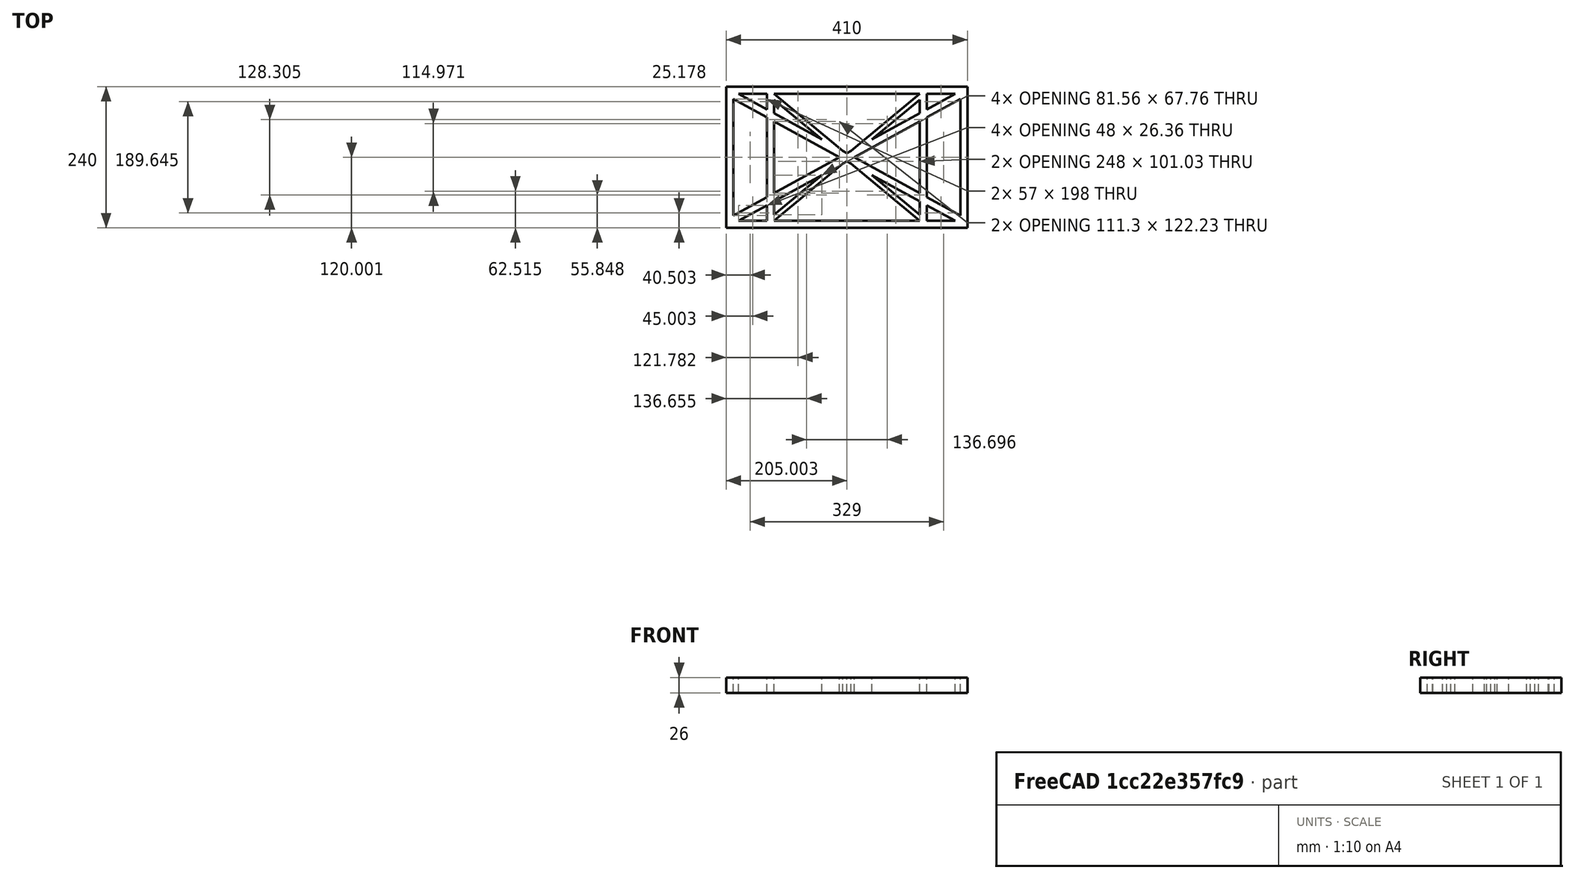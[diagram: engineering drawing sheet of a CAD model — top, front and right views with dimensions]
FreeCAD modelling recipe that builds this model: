
FCSTD DOCUMENT  (FreeCAD 0.19R0.19.2)
Label: laptopStand030
License: All rights reserved
LicenseURL: http://en.wikipedia.org/wiki/All_rights_reserved
objects: Sketcher::SketchObject×3, Part::Extrusion×1
note: 4 computed .brp shape members not serialized (recipe doc carries the construction recipe); baked Part::Feature solids carry a one-line shape summary decoded from their .brp

FEATURE [Sketcher::SketchObject] Sketch
  FullyConstrained = true
  sketch-geometry (52):
    g0: LineSegment StartX=-22.9272 StartY=136.221 StartZ=0 EndX=-22.9272 EndY=-103.779 EndZ=0
    g1: LineSegment StartX=-22.9272 StartY=136.221 StartZ=0 EndX=387.073 EndY=136.221 EndZ=0
    g2: LineSegment StartX=-22.9272 StartY=-103.779 StartZ=0 EndX=387.073 EndY=-103.779 EndZ=0
    g3: LineSegment StartX=387.073 StartY=136.221 StartZ=0 EndX=387.073 EndY=-103.779 EndZ=0
    g4: LineSegment StartX=375.073 StartY=115.221 StartZ=0 EndX=318.073 EndY=83.9235 EndZ=0
    g5: LineSegment StartX=-10.9272 StartY=-82.7794 StartZ=0 EndX=46.0728 EndY=-51.4823 EndZ=0
    g6: LineSegment StartX=-1.92719 StartY=124.221 StartZ=0 EndX=46.0728 EndY=97.8651 EndZ=0
    g7: LineSegment StartX=366.073 StartY=-91.7794 StartZ=0 EndX=318.073 EndY=-65.424 EndZ=0
    g8: LineSegment StartX=-10.9272 StartY=115.221 StartZ=0 EndX=-10.9272 EndY=-82.7794 EndZ=0
    g9: LineSegment StartX=375.073 StartY=-82.7794 StartZ=0 EndX=375.073 EndY=115.221 EndZ=0
    g10: LineSegment StartX=-1.92719 StartY=-91.7794 StartZ=0 EndX=46.0728 EndY=-91.7794 EndZ=0
    g11: LineSegment StartX=318.073 StartY=124.221 StartZ=0 EndX=366.073 EndY=124.221 EndZ=0
    g12: LineSegment StartX=306.073 StartY=-81.8102 StartZ=0 EndX=224.513 EndY=-14.0532 EndZ=0
    g13: LineSegment StartX=58.0728 StartY=114.251 StartZ=0 EndX=139.632 EndY=46.4944 EndZ=0
    g14: LineSegment StartX=306.073 StartY=124.221 StartZ=0 EndX=189.124 EndY=27.0628 EndZ=0
    g15: LineSegment StartX=58.0728 StartY=-91.7794 StartZ=0 EndX=175.022 EndY=5.37834 EndZ=0
    g16: LineSegment StartX=46.0728 StartY=124.221 StartZ=0 EndX=46.0728 EndY=97.8651 EndZ=0
    g17: LineSegment StartX=58.0728 StartY=-81.8102 StartZ=0 EndX=58.0728 EndY=-58.8351 EndZ=0
    g18: LineSegment StartX=318.073 StartY=124.221 StartZ=0 EndX=318.073 EndY=97.8651 EndZ=0
    g19: LineSegment StartX=306.073 StartY=114.251 StartZ=0 EndX=306.073 EndY=91.2763 EndZ=0
    g20: LineSegment StartX=182.073 StartY=23.1914 StartZ=0 EndX=189.124 EndY=27.0628 EndZ=0
    g21: LineSegment StartX=182.073 StartY=9.24976 StartZ=0 EndX=175.022 EndY=5.37834 EndZ=0
    g22: LineSegment StartX=224.513 StartY=46.4944 StartZ=0 EndX=306.073 EndY=114.251 EndZ=0
    g23: LineSegment StartX=175.022 StartY=27.0628 StartZ=0 EndX=58.0728 EndY=124.221 EndZ=0
    g24: LineSegment StartX=169.377 StartY=16.2206 StartZ=0 EndX=58.0728 EndY=77.3346 EndZ=0
    g25: LineSegment StartX=139.632 StartY=-14.0532 StartZ=0 EndX=58.0728 EndY=-81.8102 EndZ=0
    g26: LineSegment StartX=194.768 StartY=16.2206 StartZ=0 EndX=306.073 EndY=-44.8935 EndZ=0
    g27: LineSegment StartX=224.513 StartY=46.4944 StartZ=0 EndX=306.073 EndY=91.2763 EndZ=0
    g28: LineSegment StartX=175.022 StartY=27.0628 StartZ=0 EndX=182.073 EndY=23.1914 EndZ=0
    g29: LineSegment StartX=139.632 StartY=-14.0532 StartZ=0 EndX=58.0728 EndY=-58.8351 EndZ=0
    g30: LineSegment StartX=189.124 StartY=5.37834 StartZ=0 EndX=182.073 EndY=9.24976 EndZ=0
    g31: LineSegment StartX=189.124 StartY=5.37834 StartZ=0 EndX=306.073 EndY=-91.7794 EndZ=0
    g32: LineSegment StartX=306.073 StartY=77.3346 StartZ=0 EndX=306.073 EndY=-44.8935 EndZ=0
    g33: LineSegment StartX=318.073 StartY=83.9235 StartZ=0 EndX=318.073 EndY=-51.4823 EndZ=0
    g34: LineSegment StartX=318.073 StartY=97.8651 StartZ=0 EndX=366.073 EndY=124.221 EndZ=0
    g35: LineSegment StartX=306.073 StartY=77.3346 StartZ=0 EndX=194.768 EndY=16.2206 EndZ=0
    g36: LineSegment StartX=306.073 StartY=-58.8351 StartZ=0 EndX=224.513 EndY=-14.0532 EndZ=0
    g37: LineSegment StartX=306.073 StartY=-58.8351 StartZ=0 EndX=306.073 EndY=-81.8102 EndZ=0
    g38: LineSegment StartX=318.073 StartY=-51.4823 StartZ=0 EndX=375.073 EndY=-82.7794 EndZ=0
    g39: LineSegment StartX=318.073 StartY=-65.424 StartZ=0 EndX=318.073 EndY=-91.7794 EndZ=0
    g40: LineSegment StartX=306.073 StartY=124.221 StartZ=0 EndX=58.0728 EndY=124.221 EndZ=0
    g41: LineSegment StartX=318.073 StartY=-91.7794 StartZ=0 EndX=366.073 EndY=-91.7794 EndZ=0
    g42: LineSegment StartX=58.0728 StartY=-91.7794 StartZ=0 EndX=306.073 EndY=-91.7794 EndZ=0
    g43: LineSegment StartX=58.0728 StartY=-44.8935 StartZ=0 EndX=58.0728 EndY=77.3346 EndZ=0
    g44: LineSegment StartX=46.0728 StartY=-65.424 StartZ=0 EndX=-1.92719 EndY=-91.7794 EndZ=0
    g45: LineSegment StartX=46.0728 StartY=-65.424 StartZ=0 EndX=46.0728 EndY=-91.7794 EndZ=0
    g46: LineSegment StartX=58.0728 StartY=-44.8935 StartZ=0 EndX=169.377 EndY=16.2206 EndZ=0
    g47: LineSegment StartX=58.0728 StartY=91.2763 StartZ=0 EndX=58.0728 EndY=114.251 EndZ=0
    g48: LineSegment StartX=46.0728 StartY=83.9235 StartZ=0 EndX=46.0728 EndY=-51.4823 EndZ=0
    g49: LineSegment StartX=46.0728 StartY=124.221 StartZ=0 EndX=-1.92719 EndY=124.221 EndZ=0
    g50: LineSegment StartX=58.0728 StartY=91.2763 StartZ=0 EndX=139.632 EndY=46.4944 EndZ=0
    g51: LineSegment StartX=46.0728 StartY=83.9235 StartZ=0 EndX=-10.9272 EndY=115.221 EndZ=0
  constraints (102):
    c: Vertical(g0)
    c: Distance(g0) = 240
    c: Horizontal(g1)
    c: Distance(g1) = 410
    c: Coincident(g1,g0)
    c: Coincident(g2,g0)
    c: Horizontal(g2)
    c: Coincident(g3,g1)
    c: Vertical(g3)
    c: Coincident(g2,g3)
    c: Block(g1)
    c: Horizontal(g10)
    c: Horizontal(g11)
    c: PointOnObject(g35,g6)
    c: Coincident(g28,g20)
    c: Coincident(g30,g21)
    c: Tangent(g7,g24)
    c: PointOnObject(g24,g5)
    c: PointOnObject(g26,g4)
    c: Coincident(g20,g14)
    c: Tangent(g20,g27)
    c: Coincident(g50,g13)
    c: Coincident(g28,g23)
    c: Coincident(g22,g27)
    c: Coincident(g21,g15)
    c: Coincident(g29,g25)
    c: Tangent(g21,g29)
    c: Coincident(g36,g12)
    c: Coincident(g31,g30)
    c: Coincident(g22,g19)
    c: Tangent(g19,g32)
    c: Tangent(g18,g33)
    c: Coincident(g27,g19)
    c: Tangent(g27,g34)
    c: Coincident(g4,g33)
    c: Coincident(g35,g32)
    c: Tangent(g4,g35)
    c: Coincident(g37,g12)
    c: Tangent(g7,g36)
    c: Tangent(g32,g37)
    c: Coincident(g26,g32)
    c: Tangent(g26,g38)
    c: Coincident(g33,g38)
    c: Coincident(g39,g7)
    c: Tangent(g33,g39)
    c: Coincident(g25,g17)
    c: Tangent(g17,g43)
    c: Coincident(g29,g17)
    c: Tangent(g29,g44)
    c: Coincident(g45,g44)
    c: Tangent(g16,g45)
    c: Coincident(g5,g48)
    c: Coincident(g46,g43)
    c: Tangent(g5,g46)
    c: Tangent(g43,g47)
    c: Tangent(g16,g48)
    c: Coincident(g13,g47)
    c: PointOnObject(g40,g23)
    c: Tangent(g40,g49)
    c: Coincident(g6,g16)
    c: Coincident(g50,g47)
    c: Tangent(g6,g50)
    c: Coincident(g24,g43)
    c: Coincident(g51,g48)
    c: Tangent(g24,g51)
    c: Block(g23)
    c: Block(g14)
    c: Block(g20)
    c: Block(g40)
    c: Block(g18)
    c: Block(g34)
    c: Block(g4)
    c: Block(g38)
    c: Block(g9)
    c: Block(g36)
    c: Block(g37)
    c: Block(g7)
    c: Block(g39)
    c: Block(g22)
    c: Block(g31)
    c: Block(g42)
    c: Block(g21)
    c: Block(g15)
    c: Block(g29)
    c: Block(g25)
    c: Block(g45)
    c: Block(g44)
    c: Block(g5)
    c: Block(g8)
    c: Block(g51)
    c: Block(g6)
    c: Block(g16)
    c: Block(g13)
    c: Block(g47)
    c: Block(g35)
    c: Block(g32)
    c: Block(g24)
    c: Block(g46)
    c: Block(g49)
    c: Block(g11)
    c: Block(g41)
    c: Block(g10)
FEATURE [Part::Extrusion] Extrude
  Base = -> Sketch
  Dir = (0,0,1)
  DirMode = 2
  FaceMakerClass = Part::FaceMakerBullseye
  LengthFwd = 26
  LengthRev = 0
  Solid = true
  Symmetric = false
FEATURE [Sketcher::SketchObject] Sketch001
  FullyConstrained = true
  MapMode = 4
  Placement = pos=(0,0,0) rot=(0.57735,0.57735,0.57735;2.0944rad)
  Support = -> [Sketch]
  sketch-geometry (34):
    g0: LineSegment StartX=17.2232 StartY=-16.0875 StartZ=0 EndX=117.223 EndY=-16.0875 EndZ=0
    g1: LineSegment StartX=17.2232 StartY=-16.0875 StartZ=0 EndX=17.2232 EndY=-19.0875 EndZ=0
    g2: LineSegment StartX=117.223 StartY=-16.0875 StartZ=0 EndX=117.223 EndY=-19.0875 EndZ=0
    g3: BSplineCurve PolesCount=3 KnotsCount=2 Degree=2 IsPeriodic=0
    g4: LineSegment StartX=-9.4377 StartY=-200.664 StartZ=0 EndX=24.2583 EndY=-213.335 EndZ=0
    g5: LineSegment StartX=17.2232 StartY=-19.0875 StartZ=0 EndX=29.8094 EndY=-19.0875 EndZ=0
    g6: ArcOfCircle CenterX=73.122 CenterY=-32.2909 CenterZ=0 NormalX=0 NormalY=0 NormalZ=1 AngleXU=0 Radius=13 StartAngle=5.92268 EndAngle=9.06428
    g7: LineSegment StartX=85.2864 StartY=-36.8765 StartZ=0 EndX=78.9505 EndY=-53.7246 EndZ=0
    g8: LineSegment StartX=60.9577 StartY=-27.7052 StartZ=0 EndX=54.6191 EndY=-44.5532 EndZ=0
    g9: ArcOfCircle CenterX=66.7816 CenterY=-49.1439 CenterZ=0 NormalX=0 NormalY=0 NormalZ=1 AngleXU=0 Radius=13 StartAngle=2.78068 EndAngle=5.92131
    g10: ArcOfCircle CenterX=55.9263 CenterY=-78.1807 CenterZ=0 NormalX=0 NormalY=0 NormalZ=1 AngleXU=0 Radius=13 StartAngle=5.92268 EndAngle=9.06428
    g11: LineSegment StartX=68.0907 StartY=-82.7664 StartZ=0 EndX=61.7547 EndY=-99.6148 EndZ=0
    g12: ArcOfCircle CenterX=49.5884 CenterY=-95.0342 CenterZ=0 NormalX=0 NormalY=0 NormalZ=1 AngleXU=0 Radius=13 StartAngle=2.78068 EndAngle=5.92131
    g13: LineSegment StartX=43.7619 StartY=-73.595 StartZ=0 EndX=37.426 EndY=-90.4435 EndZ=0
    g14: ArcOfCircle CenterX=38.7206 CenterY=-124.067 CenterZ=0 NormalX=0 NormalY=0 NormalZ=1 AngleXU=0 Radius=13 StartAngle=5.92268 EndAngle=9.06428
    g15: LineSegment StartX=26.5562 StartY=-119.481 StartZ=0 EndX=20.2251 EndY=-136.329 EndZ=0
    g16: ArcOfCircle CenterX=32.3875 CenterY=-140.92 CenterZ=0 NormalX=0 NormalY=0 NormalZ=1 AngleXU=0 Radius=13 StartAngle=2.78068 EndAngle=5.92131
    g17: LineSegment StartX=50.885 StartY=-128.652 StartZ=0 EndX=44.549 EndY=-145.5 EndZ=0
    g18: ArcOfCircle CenterX=21.4715 CenterY=-169.934 CenterZ=0 NormalX=0 NormalY=0 NormalZ=1 AngleXU=0 Radius=13 StartAngle=5.92268 EndAngle=9.06428
    g19: LineSegment StartX=9.3071 StartY=-165.349 StartZ=0 EndX=2.97115 EndY=-182.197 EndZ=0
    g20: ArcOfCircle CenterX=15.1336 CenterY=-186.787 CenterZ=0 NormalX=0 NormalY=0 NormalZ=1 AngleXU=0 Radius=13 StartAngle=2.78068 EndAngle=5.92131
    g21: LineSegment StartX=33.6358 StartY=-174.52 StartZ=0 EndX=27.2999 EndY=-191.368 EndZ=0
    g22: LineSegment StartX=24.2583 StartY=-213.335 StartZ=0 EndX=25.4551 EndY=-210.153 EndZ=0
    g23: LineSegment StartX=-9.4377 StartY=-200.664 StartZ=0 EndX=-8.24091 EndY=-197.481 EndZ=0
    g24: LineSegment StartX=94.6577 StartY=-26.1351 StartZ=0 EndX=25.4551 EndY=-210.153 EndZ=0
    g25-g28: Circle x4 (B-spline internal-alignment scaffolding for g29; pole/knot coordinates omitted)
    g29: BSplineCurve PolesCount=4 KnotsCount=2 Degree=3 IsPeriodic=0
    g30: GeomPoint X=28.8094 Y=-19.0875 Z=0
    g31: GeomPoint X=47.0443 Y=-50.4712 Z=0
    g32: LineSegment StartX=47.3963 StartY=-49.5352 StartZ=0 EndX=-8.24091 EndY=-197.481 EndZ=0
    g33: Circle CenterX=53.5586 CenterY=-23.2695 CenterZ=0 NormalX=0 NormalY=0 NormalZ=1 AngleXU=0 Radius=3.24518
  constraints (63):
    c: Horizontal(g0)
    c: Distance(g0) = 100
    c: Block(g0)
    c: Coincident(g1,g0)
    c: Vertical(g1)
    c: Distance(g1) = 3
    c: Coincident(g2,g0)
    c: Vertical(g2)
    c: Distance(g2) = 3
    c: Block(g3)
    c: Coincident(g3,g2)
    c: Coincident(g5,g1)
    c: Horizontal(g5)
    c: Block(g6)
    c: Distance(g7) = 18
    c: Coincident(g7,g6)
    c: Coincident(g8,g6)
    c: Block(g9)
    c: Coincident(g9,g8)
    c: Block(g8)
    c: Coincident(g11,g10)
    c: Coincident(g13,g10)
    c: Block(g12)
    c: Coincident(g12,g13)
    c: Block(g13)
    c: Block(g10)
    c: Block(g11)
    c: Coincident(g17,g14)
    c: Coincident(g15,g14)
    c: Block(g16)
    c: Coincident(g16,g15)
    c: Block(g15)
    c: Block(g14)
    c: Coincident(g21,g18)
    c: Coincident(g19,g18)
    c: Block(g20)
    c: Coincident(g20,g19)
    c: Block(g19)
    c: Block(g18)
    c: Distance(g21) = 18
    c: Block(g21)
    c: Block(g17)
    c: Distance(g22) = 3.4
    c: Coincident(g23,g4)
    c: Coincident(g24,g3)
    c: Coincident(g24,g22)
    c: Coincident(g32,g23)
    c: Block(g24)
    c: Block(g4)
    c: Block(g22)
    c: Block(g7)
    c: Weight(g25) = 1
    c: Equal(g25,g26)
    c: Equal(g25,g27)
    c: Equal(g25,g28)
    c: InternalAlignment(g25-g28 -> g29) x4
    c: InternalAlignment(g30,g29)
    c: InternalAlignment(g31,g29)
    c: PointOnObject(g32,g28)
    c: PointOnObject(g5,g25)
    c: Block(g29)
    c: Block(g32)
    c: Block(g33)
FEATURE [Sketcher::SketchObject] Sketch002
  FullyConstrained = true
  Placement = pos=(0,0,0) rot=(-1,0,0;4.71239rad)
